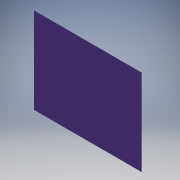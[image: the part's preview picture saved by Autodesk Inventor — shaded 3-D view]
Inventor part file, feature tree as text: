
AUTODESK INVENTOR PART (.ipt)
format: ipt  version: 2018 (Build 220112000, 112)  size: 98,816 bytes
history: native  units: mm
features: extrude x1, chamfer x1, sketch x1
ambient origin geometry x8: Origin, YZ Plane, XZ Plane, XY Plane, X Axis, Y Axis, Z Axis, Center Point
bodies: Volumenkörper1 (feature_tree)
feature tree (3):
  extrude  "Extrusion1"  Depth=20.0mm
  chamfer  "Fase1"  Distance=20.0mm
  sketch  "Skizze1"  dims[d0=500.0mm d1=400.0mm d2=20.0mm d3=0.0mm d4=20.0mm d5=2.0mm d6=45.0deg]
